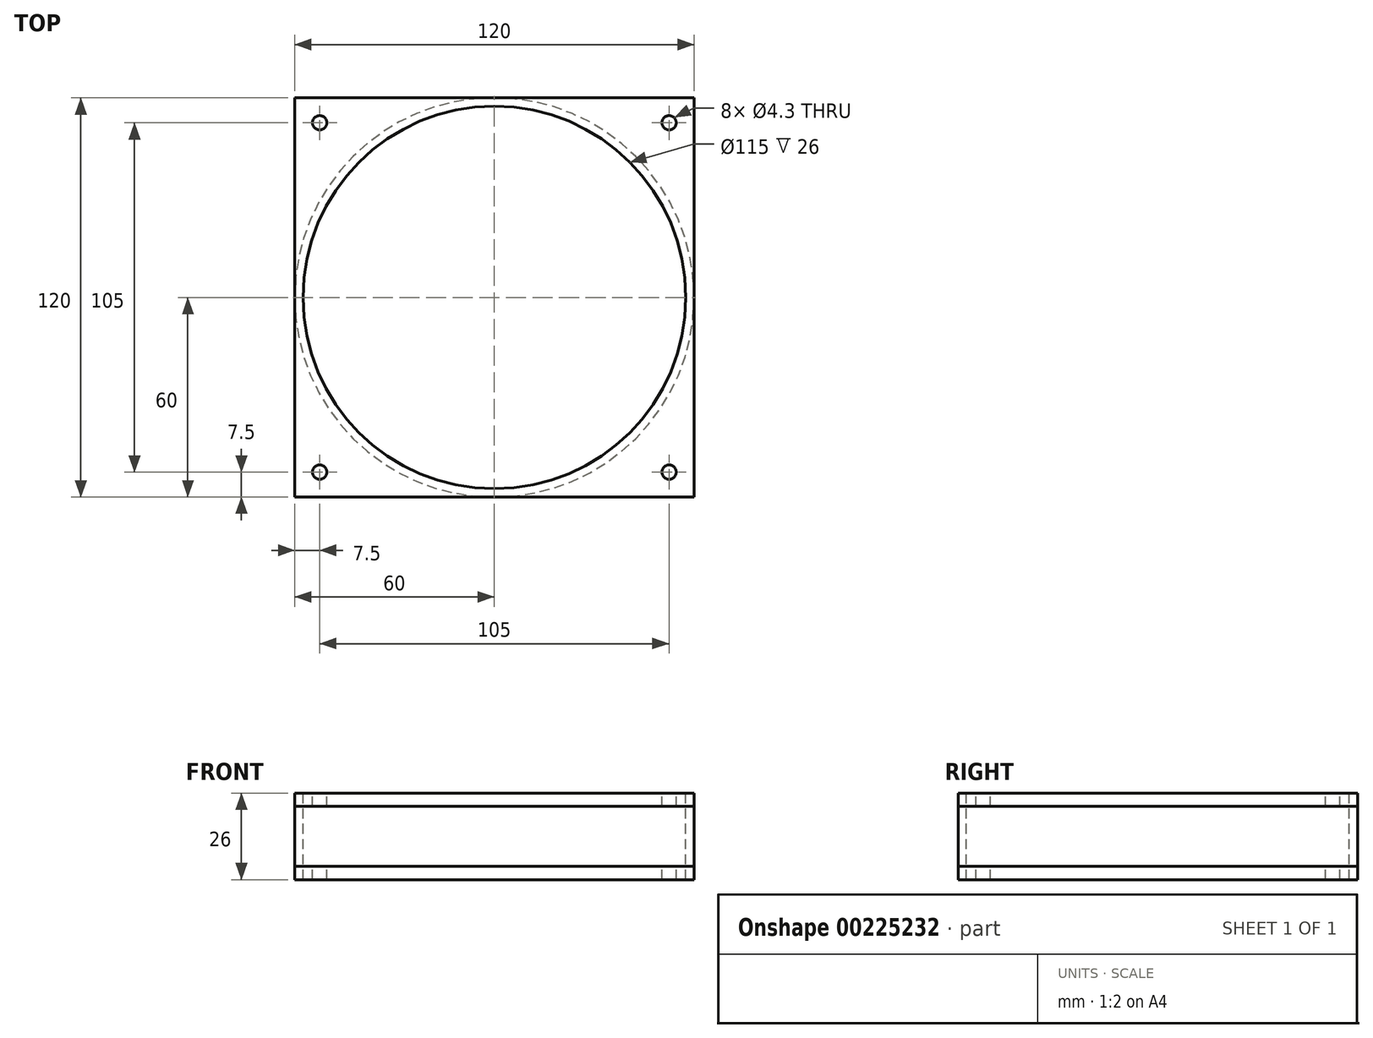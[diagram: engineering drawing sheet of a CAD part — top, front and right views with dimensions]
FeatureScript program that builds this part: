
annotation { "Feature Type Name" : "Feature", "Feature Type Description" : "" }
export const myFeature = defineFeature(function(context is Context, id is Id, definition is map)
    precondition{}
    {
        {
            var Q0;
            Q0=qCreatedBy(makeId("Top.planeOp"),FACE);
            var sketch = newSketch(context, id + "F0", { "sketchPlane" : qUnion([Q0])});
            skLineSegment(sketch, "E0.bottom", {"start": v(60, -60) * mm, "end": v(-60, -60) * mm});
            skLineSegment(sketch, "E0.top", {"start": v(60, 60) * mm, "end": v(-60, 60) * mm});
            skLineSegment(sketch, "E0.left", {"start": v(60, -60) * mm, "end": v(60, 60) * mm});
            skLineSegment(sketch, "E0.right", {"start": v(-60, -60) * mm, "end": v(-60, 60) * mm});
            skPoint(sketch, "E0.middle", {"position": v(0, 0) * mm});
            skSolve(sketch);
        }
        {
            var Q0;
            Q0 = qSketchRegion(id + "F0", true);
            extrude(context, id + "F1", {"entities" : qUnion([Q0]), "depth" : 26 * mm});
        }
        {
            var Q0;
            Q0=makeQuery(id+"F1.opExtrude","CAP_FACE",FACE,{"disambiguationData":[OSD([sQuery(id+"F0.wireOp",EDGE,"E0.bottom"),sQuery(id+"F0.wireOp",EDGE,"E0.top"),sQuery(id+"F0.wireOp",EDGE,"E0.left"),sQuery(id+"F0.wireOp",EDGE,"E0.right")])],"isStart":false});
            var sketch = newSketch(context, id + "F2", { "sketchPlane" : qUnion([Q0])});
            skCircle(sketch, "E1", {"center": v(0, 0) * mm, "radius": 57.5 * mm});
            skSolve(sketch);
        }
        {
            var Q0;
            Q0 = qSketchRegion(id + "F2", true);
            extrude(context, id + "F3", {"entities" : qUnion([Q0]), "operationType" : NewBodyOperationType.REMOVE, "endBound" : BoundingType.THROUGH_ALL, "oppositeDirection" : true, "depth" : 25 * mm});
        }
        {
            var Q0;
            Q0=qCreatedBy(makeId("Top.planeOp"),FACE);
            cPlane(context, id + "F4", {"entities" : qUnion([Q0]), "cplaneType" : CPlaneType.OFFSET, "offset" : 4 * mm, "width" : 150 * mm, "height" : 150 * mm});
        }
        {
            var Q0;
            Q0=qCreatedBy(id+"F4.planeOp",FACE);
            var sketch = newSketch(context, id + "F5", { "sketchPlane" : qUnion([Q0])});
            skCircle(sketch, "E2.0", {"center": v(0, 0) * mm, "radius": 57.5 * mm, "construction": true});
            skCircle(sketch, "E3.0", {"center": v(0, 0) * mm, "radius": 60 * mm});
            skLineSegment(sketch, "E4.0.0", {"start": v(60, -60) * mm, "end": v(60, 60) * mm, "construction": true});
            skLineSegment(sketch, "E4.0.1", {"start": v(60, 60) * mm, "end": v(-60, 60) * mm, "construction": true});
            skLineSegment(sketch, "E4.0.2", {"start": v(-60, 60) * mm, "end": v(-60, -60) * mm, "construction": true});
            skLineSegment(sketch, "E4.0.3", {"start": v(-60, -60) * mm, "end": v(60, -60) * mm, "construction": true});
            skLineSegment(sketch, "E5", {"start": v(0, 60) * mm, "end": v(-60, 60) * mm, "construction": true});
            skLineSegment(sketch, "E6", {"start": v(-60, 60) * mm, "end": v(-60, 0) * mm, "construction": true});
            skLineSegment(sketch, "E7", {"start": v(-60, 60) * mm, "end": v(-60, -60) * mm});
            skLineSegment(sketch, "E8", {"start": v(-60, -60) * mm, "end": v(60, -60) * mm});
            skLineSegment(sketch, "E9", {"start": v(60, -60) * mm, "end": v(60, 60) * mm});
            skLineSegment(sketch, "E10", {"start": v(60, 60) * mm, "end": v(0, 60) * mm});
            skLineSegment(sketch, "E11", {"start": v(0, 60) * mm, "end": v(-60, 60) * mm});
            skSolve(sketch);
        }
        {
            var Q0;
            {var subQ0=sQuery(id+"F5.wireOp",EDGE,"E10");Q0=makeQuery(id+"F5.imprint","IMPRINT",FACE,{"disambiguationData":[TD([[makeQuery(id+"F5.imprint","IMPRINT",EDGE,{"derivedFrom":subQ0}),1.0]])]});}
            var Q1;
            {var subQ0=sQuery(id+"F5.wireOp",EDGE,"E9");var subQ1=sQuery(id+"F5.wireOp",EDGE,"E3.0");var subQ2=makeQuery(id+"F5.imprint","INTERSECT",VERTEX,{"derivedFrom":[subQ1,subQ0]});Q1=makeQuery(id+"F5.imprint","IMPRINT",FACE,{"disambiguationData":[TD([[makeQuery(id+"F5.imprint","IMPRINT",EDGE,{"disambiguationData":[TD([[subQ2,1.0]])],"derivedFrom":subQ1}),-1.0]])]});}
            var Q2;
            {var subQ0=sQuery(id+"F5.wireOp",EDGE,"E7");var subQ1=sQuery(id+"F5.wireOp",EDGE,"E3.0");var subQ2=makeQuery(id+"F5.imprint","INTERSECT",VERTEX,{"derivedFrom":[subQ1,subQ0]});Q2=makeQuery(id+"F5.imprint","IMPRINT",FACE,{"disambiguationData":[TD([[makeQuery(id+"F5.imprint","IMPRINT",EDGE,{"disambiguationData":[TD([[subQ2,-1.0]])],"derivedFrom":subQ1}),-1.0]])]});}
            var Q3;
            {var subQ0=sQuery(id+"F5.wireOp",EDGE,"E11");Q3=makeQuery(id+"F5.imprint","IMPRINT",FACE,{"disambiguationData":[TD([[makeQuery(id+"F5.imprint","IMPRINT",EDGE,{"derivedFrom":subQ0}),1.0]])]});}
            extrude(context, id + "F6", {"entities" : qUnion([Q0, Q1, Q2, Q3]), "operationType" : NewBodyOperationType.REMOVE, "depth" : 18 * mm});
        }
        {
            var Q0;
            Q0=makeQuery(id+"F1.opExtrude","CAP_FACE",FACE,{"disambiguationData":[OSD([sQuery(id+"F0.wireOp",EDGE,"E0.bottom"),sQuery(id+"F0.wireOp",EDGE,"E0.top"),sQuery(id+"F0.wireOp",EDGE,"E0.left"),sQuery(id+"F0.wireOp",EDGE,"E0.right")])],"isStart":false});
            var sketch = newSketch(context, id + "F7", { "sketchPlane" : qUnion([Q0])});
            skCircle(sketch, "E12", {"center": v(-52.5, 52.5) * mm, "radius": 2.15 * mm});
            skCircle(sketch, "E13", {"center": v(52.5, 52.5) * mm, "radius": 2.15 * mm});
            skCircle(sketch, "E14", {"center": v(52.5, -52.5) * mm, "radius": 2.15 * mm});
            skCircle(sketch, "E15", {"center": v(-52.5, -52.5) * mm, "radius": 2.15 * mm});
            skSolve(sketch);
        }
        {
            var Q0;
            Q0 = qSketchRegion(id + "F7", true);
            extrude(context, id + "F8", {"entities" : qUnion([Q0]), "operationType" : NewBodyOperationType.REMOVE, "endBound" : BoundingType.THROUGH_ALL, "oppositeDirection" : true, "depth" : 25 * mm});
        }
    });
